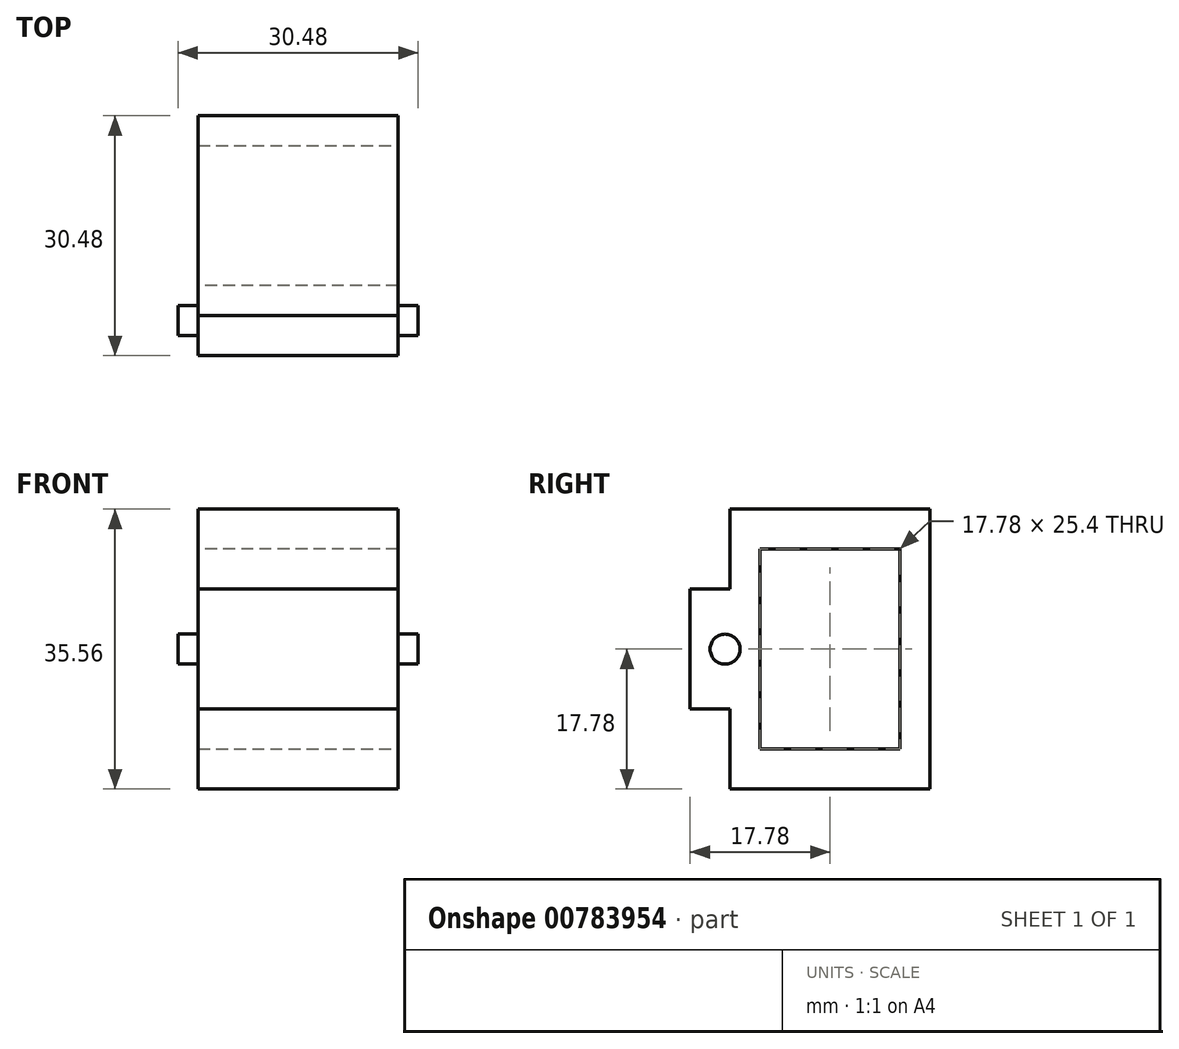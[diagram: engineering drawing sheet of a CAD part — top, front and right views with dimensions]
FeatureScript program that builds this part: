
annotation { "Feature Type Name" : "Feature", "Feature Type Description" : "" }
export const myFeature = defineFeature(function(context is Context, id is Id, definition is map)
    precondition{}
    {
        {
            var Q0;
            Q0=qCreatedBy(makeId("Top.planeOp"),FACE);
            var sketch = newSketch(context, id + "F0", { "sketchPlane" : qUnion([Q0])});
            skLineSegment(sketch, "E0", {"start": v(0, 0) * mm, "end": v(0, -17.78) * mm});
            skLineSegment(sketch, "E1", {"start": v(0, 0) * mm, "end": v(0, 7.62) * mm});
            skLineSegment(sketch, "E2", {"start": v(0, 0) * mm, "end": v(-25.4, 0) * mm});
            skLineSegment(sketch, "E3", {"start": v(-25.4, 0) * mm, "end": v(-25.4, -17.78) * mm});
            skLineSegment(sketch, "E4", {"start": v(-25.4, 0) * mm, "end": v(-25.4, 7.62) * mm});
            skLineSegment(sketch, "E5", {"start": v(-25.4, -17.78) * mm, "end": v(0, -17.78) * mm});
            skLineSegment(sketch, "E6", {"start": v(-25.4, 7.62) * mm, "end": v(0, 7.62) * mm});
            skSolve(sketch);
        }
        {
            var Q0;
            Q0 = qSketchRegion(id + "F0", true);
            extrude(context, id + "F1", {"entities" : qUnion([Q0]), "depth" : 5.08 * mm, "offsetDistance" : 25.4 * mm});
        }
        {
            var Q0;
            Q0=makeQuery(id+"F1.opExtrude","CAP_FACE",FACE,{"disambiguationData":[OSD([sQuery(id+"F0.wireOp",EDGE,"E0"),sQuery(id+"F0.wireOp",EDGE,"E1"),sQuery(id+"F0.wireOp",EDGE,"E3"),sQuery(id+"F0.wireOp",EDGE,"E4"),sQuery(id+"F0.wireOp",EDGE,"E5"),sQuery(id+"F0.wireOp",EDGE,"E6")])],"isStart":false});
            var sketch = newSketch(context, id + "F2", { "sketchPlane" : qUnion([Q0])});
            skLineSegment(sketch, "E7", {"start": v(0, -17.78) * mm, "end": v(0, -13.97) * mm});
            skLineSegment(sketch, "E8", {"start": v(0, -13.97) * mm, "end": v(-25.4, -13.97) * mm});
            skLineSegment(sketch, "E9", {"start": v(-25.4, -13.97) * mm, "end": v(-25.4, -17.78) * mm});
            skLineSegment(sketch, "E10", {"start": v(-25.4, -17.78) * mm, "end": v(0, -17.78) * mm});
            skLineSegment(sketch, "E11", {"start": v(-25.4, 7.62) * mm, "end": v(-25.4, 3.8) * mm});
            skLineSegment(sketch, "E12", {"start": v(-25.4, 3.8) * mm, "end": v(0, 3.8) * mm});
            skLineSegment(sketch, "E13", {"start": v(0, 3.8) * mm, "end": v(0, 7.62) * mm});
            skLineSegment(sketch, "E14", {"start": v(0, 7.62) * mm, "end": v(-25.4, 7.62) * mm});
            skSolve(sketch);
        }
        {
            var Q0;
            Q0 = qSketchRegion(id + "F2", true);
            extrude(context, id + "F3", {"entities" : qUnion([Q0]), "operationType" : NewBodyOperationType.ADD, "depth" : 25.4 * mm, "offsetDistance" : 25.4 * mm});
        }
        {
            var Q0;
            Q0=makeQuery(id+"F3.opExtrude","CAP_FACE",FACE,{"disambiguationData":[OSD([sQuery(id+"F2.wireOp",EDGE,"E7"),sQuery(id+"F2.wireOp",EDGE,"E8"),sQuery(id+"F2.wireOp",EDGE,"E9"),sQuery(id+"F2.wireOp",EDGE,"E10")])],"isStart":false});
            var sketch = newSketch(context, id + "F4", { "sketchPlane" : qUnion([Q0])});
            skLineSegment(sketch, "E15", {"start": v(0, -17.78) * mm, "end": v(0, 7.62) * mm});
            skLineSegment(sketch, "E16", {"start": v(0, -17.78) * mm, "end": v(-25.4, -17.78) * mm});
            skLineSegment(sketch, "E17", {"start": v(-25.4, -17.78) * mm, "end": v(-25.4, 7.62) * mm});
            skLineSegment(sketch, "E18", {"start": v(-25.4, 7.62) * mm, "end": v(0, 7.62) * mm});
            skSolve(sketch);
        }
        {
            var Q0;
            Q0 = qSketchRegion(id + "F4", true);
            extrude(context, id + "F5", {"entities" : qUnion([Q0]), "operationType" : NewBodyOperationType.ADD, "depth" : 5.08 * mm, "offsetDistance" : 25.4 * mm});
        }
        {
            var Q0;
            Q0=makeQuery(id+"F5.boolean.opBoolean","MERGE",FACE,{"derivedFrom":[makeQuery(id+"F3.boolean.opBoolean","MERGE",FACE,{"derivedFrom":[makeQuery(id+"F1.opExtrude","SWEPT_FACE",FACE,{"disambiguationData":[OSD([sQuery(id+"F0.wireOp",EDGE,"E5")])]}),makeQuery(id+"F3.opExtrude","SWEPT_FACE",FACE,{"disambiguationData":[OSD([sQuery(id+"F2.wireOp",EDGE,"E10")])]})]}),makeQuery(id+"F5.opExtrude","SWEPT_FACE",FACE,{"disambiguationData":[OSD([sQuery(id+"F4.wireOp",EDGE,"E16")])]})]});
            var sketch = newSketch(context, id + "F6", { "sketchPlane" : qUnion([Q0])});
            skLineSegment(sketch, "E19", {"start": v(-25.4, 35.56) * mm, "end": v(-25.4, 25.4) * mm});
            skLineSegment(sketch, "E20", {"start": v(-25.4, 0) * mm, "end": v(-25.4, 10.16) * mm});
            skLineSegment(sketch, "E21", {"start": v(0, 35.56) * mm, "end": v(0, 25.4) * mm});
            skLineSegment(sketch, "E22", {"start": v(0, 0) * mm, "end": v(0, 10.16) * mm});
            skLineSegment(sketch, "E23", {"start": v(-25.4, 25.4) * mm, "end": v(0, 25.4) * mm});
            skLineSegment(sketch, "E24", {"start": v(0, 10.16) * mm, "end": v(-25.4, 10.16) * mm});
            skLineSegment(sketch, "E25", {"start": v(-25.4, 25.4) * mm, "end": v(-25.4, 10.16) * mm});
            skLineSegment(sketch, "E26", {"start": v(0, 10.16) * mm, "end": v(0, 25.4) * mm});
            skSolve(sketch);
        }
        {
            var Q0;
            Q0 = qSketchRegion(id + "F6", true);
            extrude(context, id + "F7", {"entities" : qUnion([Q0]), "operationType" : NewBodyOperationType.ADD, "depth" : 5.08 * mm, "offsetDistance" : 25.4 * mm});
        }
        {
            var Q0;
            Q0=makeQuery(id+"F7.boolean.opBoolean","MERGE",FACE,{"derivedFrom":[makeQuery(id+"F5.boolean.opBoolean","MERGE",FACE,{"derivedFrom":[makeQuery(id+"F3.boolean.opBoolean","MERGE",FACE,{"derivedFrom":[makeQuery(id+"F1.opExtrude","SWEPT_FACE",FACE,{"disambiguationData":[OSD([sQuery(id+"F0.wireOp",EDGE,"E0"),sQuery(id+"F0.wireOp",EDGE,"E1")])]}),makeQuery(id+"F3.opExtrude","SWEPT_FACE",FACE,{"disambiguationData":[OSD([sQuery(id+"F2.wireOp",EDGE,"E7")])]}),makeQuery(id+"F3.opExtrude","SWEPT_FACE",FACE,{"disambiguationData":[OSD([sQuery(id+"F2.wireOp",EDGE,"E13")])]})]}),makeQuery(id+"F5.opExtrude","SWEPT_FACE",FACE,{"disambiguationData":[OSD([sQuery(id+"F4.wireOp",EDGE,"E15")])]})]}),makeQuery(id+"F7.opExtrude","SWEPT_FACE",FACE,{"disambiguationData":[OSD([sQuery(id+"F6.wireOp",EDGE,"E26")])]})]});
            var sketch = newSketch(context, id + "F8", { "sketchPlane" : qUnion([Q0])});
            skLineSegment(sketch, "E27", {"start": v(-22.86, 17.78) * mm, "end": v(-13.97, 17.78) * mm});
            skLineSegment(sketch, "E28", {"start": v(-13.97, 17.78) * mm, "end": v(-18.41, 17.78) * mm});
            skCircle(sketch, "E29", {"center": v(-18.41, 17.78) * mm, "radius": 1.9 * mm});
            skSolve(sketch);
        }
        {
            var Q0;
            Q0 = qSketchRegion(id + "F8", true);
            extrude(context, id + "F9", {"entities" : qUnion([Q0]), "operationType" : NewBodyOperationType.ADD, "depth" : 2.54 * mm, "offsetDistance" : 25.4 * mm});
        }
        {
            var Q0;
            Q0=makeQuery(id+"F7.boolean.opBoolean","MERGE",FACE,{"derivedFrom":[makeQuery(id+"F5.boolean.opBoolean","MERGE",FACE,{"derivedFrom":[makeQuery(id+"F3.boolean.opBoolean","MERGE",FACE,{"derivedFrom":[makeQuery(id+"F1.opExtrude","SWEPT_FACE",FACE,{"disambiguationData":[OSD([sQuery(id+"F0.wireOp",EDGE,"E3"),sQuery(id+"F0.wireOp",EDGE,"E4")])]}),makeQuery(id+"F3.opExtrude","SWEPT_FACE",FACE,{"disambiguationData":[OSD([sQuery(id+"F2.wireOp",EDGE,"E9")])]}),makeQuery(id+"F3.opExtrude","SWEPT_FACE",FACE,{"disambiguationData":[OSD([sQuery(id+"F2.wireOp",EDGE,"E11")])]})]}),makeQuery(id+"F5.opExtrude","SWEPT_FACE",FACE,{"disambiguationData":[OSD([sQuery(id+"F4.wireOp",EDGE,"E17")])]})]}),makeQuery(id+"F7.opExtrude","SWEPT_FACE",FACE,{"disambiguationData":[OSD([sQuery(id+"F6.wireOp",EDGE,"E25")])]})]});
            var sketch = newSketch(context, id + "F10", { "sketchPlane" : qUnion([Q0])});
            skLineSegment(sketch, "E30", {"start": v(22.86, 17.78) * mm, "end": v(13.97, 17.78) * mm});
            skLineSegment(sketch, "E31", {"start": v(13.97, 17.78) * mm, "end": v(18.41, 17.78) * mm});
            skCircle(sketch, "E32", {"center": v(18.41, 17.78) * mm, "radius": 1.9 * mm});
            skSolve(sketch);
        }
        {
            var Q0;
            Q0 = qSketchRegion(id + "F10", true);
            extrude(context, id + "F11", {"entities" : qUnion([Q0]), "operationType" : NewBodyOperationType.ADD, "depth" : 2.54 * mm, "offsetDistance" : 25.4 * mm});
        }
    });
